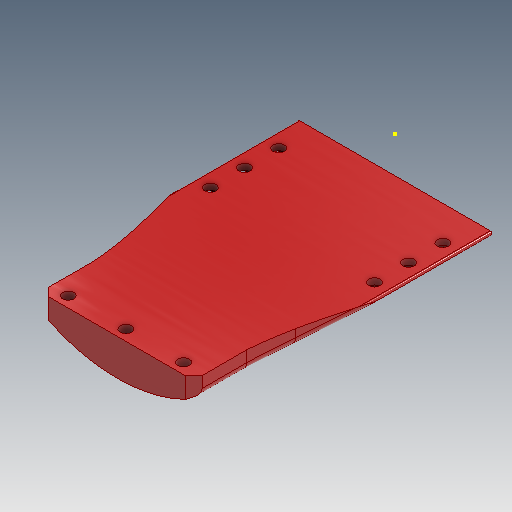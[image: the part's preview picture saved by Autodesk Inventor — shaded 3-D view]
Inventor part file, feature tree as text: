
AUTODESK INVENTOR PART (.ipt)
format: ipt  version: 2020.3 (Build 243373010, 373A)  size: 506,368 bytes
history: native  units: mm
features: extrude x6, mirror x4, sketch x4, plane x3, chamfer x1, fillet x1, pattern_linear x1, delete_face x1, projected_geometry x1
ambient origin geometry x8: Origin, YZ Plane, XZ Plane, XY Plane, X Axis, Y Axis, Z Axis, Center Point
bodies: Solid1 (feature_tree)
feature tree (22):
  extrude  "Extrusion1"  Depth=325.038mm TaperAngle=0.0deg
  extrude  "Extrusion2"  [1 undecoded]
  mirror  "Mirror1"
  plane  "Work Plane1"
  extrude  "Extrusion3"  Depth=10.0mm TaperAngle=45.0deg
  chamfer  "Chamfer2"  Distance=10.0mm
  fillet  "Fillet2"  Radius=21.0mm
  mirror  "Mirror2"
  sketch  "Sketch4"  dims[d7=42.508mm d8=0.0mm d12=10.0mm d13=2.0mm d14=45.0deg]
  mirror  "Mirror3"
  sketch  "Sketch5"  dims[d16=2.0mm d17=10.0mm d18=21.0mm d19=21.0mm d20=21.0mm d21=21.0mm d22=21.0mm d23=21.0mm d24=21.0mm d25=21.0mm d26=21.0mm d27=23.846mm d28=0.0mm d29=35.213mm d30=0.0mm d31=30.0mm d33=40.0mm d34=14.19mm d35=0.0mm]
  extrude  "Extrusion4"  Depth=10.0mm
  extrude  "Extrusion5"  Depth=10.0mm
  mirror  "Mirror4"
  pattern_linear  "Rectangular Pattern1"  Spacing1=21.0mm  [1 undecoded]
  delete_face  "Delete Face1"
  extrude  "Extrusion6"  Depth=10.0mm
  sketch  "Sketch2"  dims[d0=234.147mm d2=325.038mm d3=0.0mm]
  sketch  "Sketch3"  dims[d4=0.0mm d5=0.0mm d6=-42.5mm]
  plane  "Work Plane2"
  plane  "Work Plane3"
  projected_geometry  "Projected Loop2"
note: 2 required parameter values undecoded (feature->parameter linkage not recoverable at this tier; creation-order binding heuristic only, values carry confidence <= 0.55)
